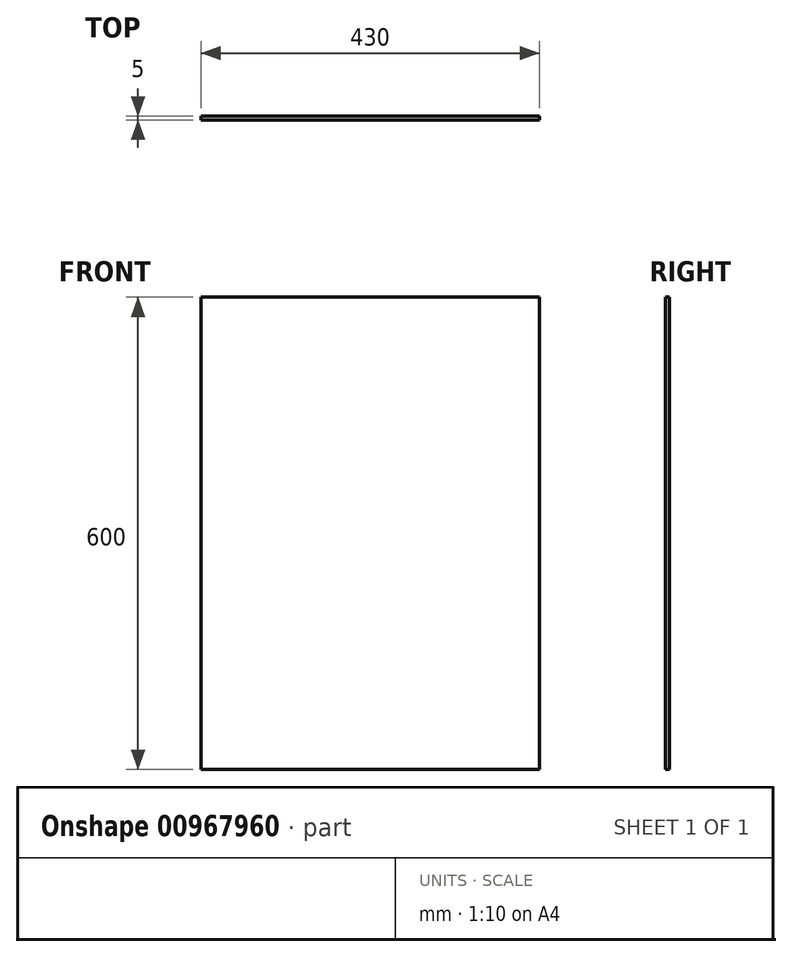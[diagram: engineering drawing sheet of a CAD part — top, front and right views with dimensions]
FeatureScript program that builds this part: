
annotation { "Feature Type Name" : "Feature", "Feature Type Description" : "" }
export const myFeature = defineFeature(function(context is Context, id is Id, definition is map)
    precondition{}
    {
        {
            var Q0;
            Q0=qCreatedBy(makeId("Front.planeOp"),FACE);
            var sketch = newSketch(context, id + "F0", { "sketchPlane" : qUnion([Q0])});
            skLineSegment(sketch, "E0.bottom", {"start": v(215, -300) * mm, "end": v(-215, -300) * mm});
            skLineSegment(sketch, "E0.top", {"start": v(215, 300) * mm, "end": v(-215, 300) * mm});
            skLineSegment(sketch, "E0.left", {"start": v(215, -300) * mm, "end": v(215, 300) * mm});
            skLineSegment(sketch, "E0.right", {"start": v(-215, -300) * mm, "end": v(-215, 300) * mm});
            skPoint(sketch, "E0.middle", {"position": v(0, 0) * mm});
            skSolve(sketch);
        }
        {
            var Q0;
            Q0 = qSketchRegion(id + "F0", true);
            extrude(context, id + "F1", {"entities" : qUnion([Q0]), "depth" : 5 * mm, "offsetDistance" : 25 * mm});
        }
    });
